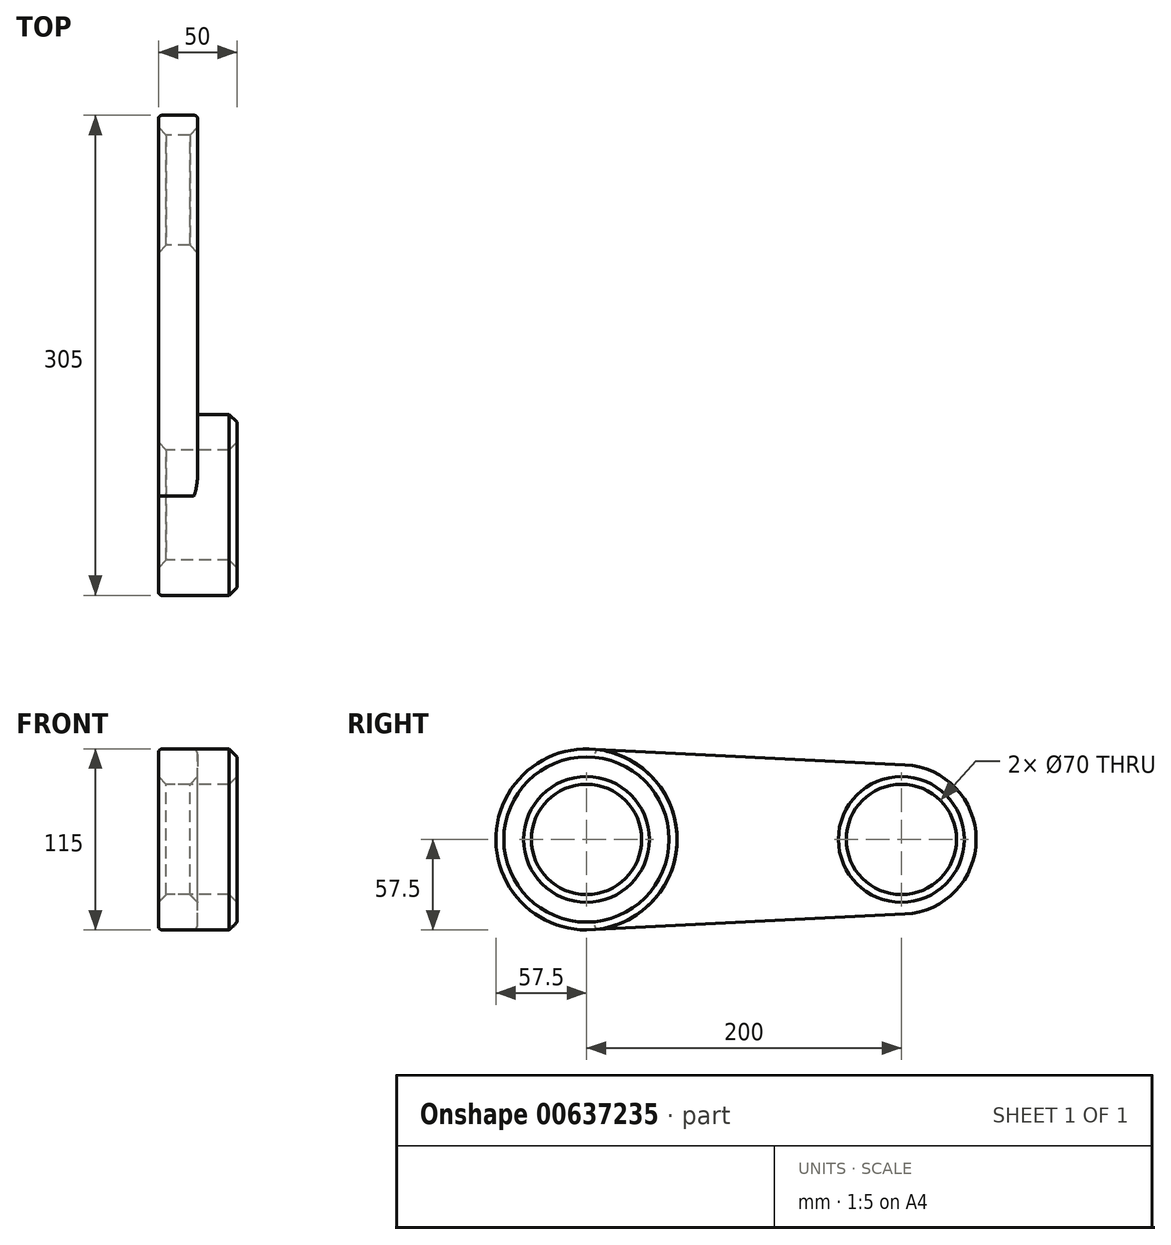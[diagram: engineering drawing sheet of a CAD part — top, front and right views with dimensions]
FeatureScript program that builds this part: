
annotation { "Feature Type Name" : "Feature", "Feature Type Description" : "" }
export const myFeature = defineFeature(function(context is Context, id is Id, definition is map)
    precondition{}
    {
        {
            var Q0;
            Q0=qCreatedBy(makeId("Right.planeOp"),FACE);
            var sketch = newSketch(context, id + "F0", { "sketchPlane" : qUnion([Q0])});
            skCircle(sketch, "E0", {"center": v(0, 0) * mm, "radius": 57.5 * mm});
            skCircle(sketch, "E1", {"center": v(200, 0) * mm, "radius": 47.5 * mm});
            skLineSegment(sketch, "E2", {"start": v(0, 57.5) * mm, "end": v(202.36, 47.44) * mm});
            skLineSegment(sketch, "E3", {"start": v(202.36, 47.44) * mm, "end": v(202.36, 47.44) * mm});
            skLineSegment(sketch, "E4", {"start": v(0, -57.5) * mm, "end": v(202.36, -47.44) * mm});
            skCircle(sketch, "E5", {"center": v(0, 0) * mm, "radius": 35 * mm});
            skCircle(sketch, "E6", {"center": v(200, 0) * mm, "radius": 35 * mm});
            skSolve(sketch);
        }
        {
            var Q0;
            Q0 = qSketchRegion(id + "F0", true);
            extrude(context, id + "F1", {"entities" : qUnion([Q0]), "depth" : 25 * mm, "offsetDistance" : 25 * mm});
        }
        {
            var Q0;
            Q0=qCreatedBy(makeId("Right.planeOp"),FACE);
            var sketch = newSketch(context, id + "F2", { "sketchPlane" : qUnion([Q0])});
            skCircle(sketch, "E7", {"center": v(0, 0) * mm, "radius": 57.5 * mm});
            skCircle(sketch, "E8", {"center": v(0, 0) * mm, "radius": 35 * mm});
            skSolve(sketch);
        }
        {
            var Q0;
            Q0 = qSketchRegion(id + "F2", true);
            extrude(context, id + "F3", {"entities" : qUnion([Q0]), "operationType" : NewBodyOperationType.ADD, "depth" : 50 * mm, "offsetDistance" : 25 * mm});
        }
        {
            var Q0;
            Q0=makeQuery(id+"F3.opExtrude","CAP_EDGE",EDGE,{"disambiguationData":[OSD([sQuery(id+"F2.wireOp",EDGE,"E8")])],"isStart":false});
            var Q1;
            Q1=makeQuery(id+"F3.opExtrude","CAP_EDGE",EDGE,{"disambiguationData":[OSD([sQuery(id+"F2.wireOp",EDGE,"E7")])],"isStart":false});
            var Q2;
            Q2=makeQuery(id+"F1.opExtrude","CAP_EDGE",EDGE,{"disambiguationData":[OSD([sQuery(id+"F0.wireOp",EDGE,"E6")])],"isStart":false});
            chamfer(context, id + "F4", {"entities" : qUnion([Q0, Q1, Q2]), "width" : 5 * mm, "tangentPropagation" : true});
        }
        {
            var Q0;
            Q0=makeQuery(id+"F1.opExtrude","CAP_EDGE",EDGE,{"disambiguationData":[OSD([sQuery(id+"F0.wireOp",EDGE,"E6")])],"isStart":true});
            var Q1;
            Q1=makeQuery(id+"F1.opExtrude","CAP_EDGE",EDGE,{"disambiguationData":[OSD([sQuery(id+"F0.wireOp",EDGE,"E5")])],"isStart":true});
            chamfer(context, id + "F5", {"entities" : qUnion([Q0, Q1]), "width" : 5 * mm, "tangentPropagation" : true});
        }
        {
            var Q0;
            Q0=makeQuery(id+"F1.opExtrude","CAP_EDGE",EDGE,{"disambiguationData":[OSD([sQuery(id+"F0.wireOp",EDGE,"E0")])],"isStart":true});
            var Q1;
            Q1=makeQuery(id+"F1.opExtrude","CAP_EDGE",EDGE,{"disambiguationData":[OSD([sQuery(id+"F0.wireOp",EDGE,"E4")])],"isStart":true});
            var Q2;
            Q2=makeQuery(id+"F1.opExtrude","CAP_EDGE",EDGE,{"disambiguationData":[OSD([sQuery(id+"F0.wireOp",EDGE,"E2")])],"isStart":true});
            var Q3;
            Q3=makeQuery(id+"F1.opExtrude","CAP_EDGE",EDGE,{"disambiguationData":[OSD([sQuery(id+"F0.wireOp",EDGE,"E1")])],"isStart":true});
            var Q4;
            Q4=makeQuery(id+"F1.opExtrude","CAP_EDGE",EDGE,{"disambiguationData":[OSD([sQuery(id+"F0.wireOp",EDGE,"E2")])],"isStart":false});
            var Q5;
            Q5=makeQuery(id+"F1.opExtrude","CAP_EDGE",EDGE,{"disambiguationData":[OSD([sQuery(id+"F0.wireOp",EDGE,"E1")])],"isStart":false});
            var Q6;
            Q6=makeQuery(id+"F1.opExtrude","CAP_EDGE",EDGE,{"disambiguationData":[OSD([sQuery(id+"F0.wireOp",EDGE,"E4")])],"isStart":false});
            fillet(context, id + "F6", {"entities" : qUnion([Q0, Q1, Q2, Q3, Q4, Q5, Q6]), "radius" : 2.5 * mm, "tangentPropagation" : true, "allowEdgeOverflow" : false});
        }
    });
